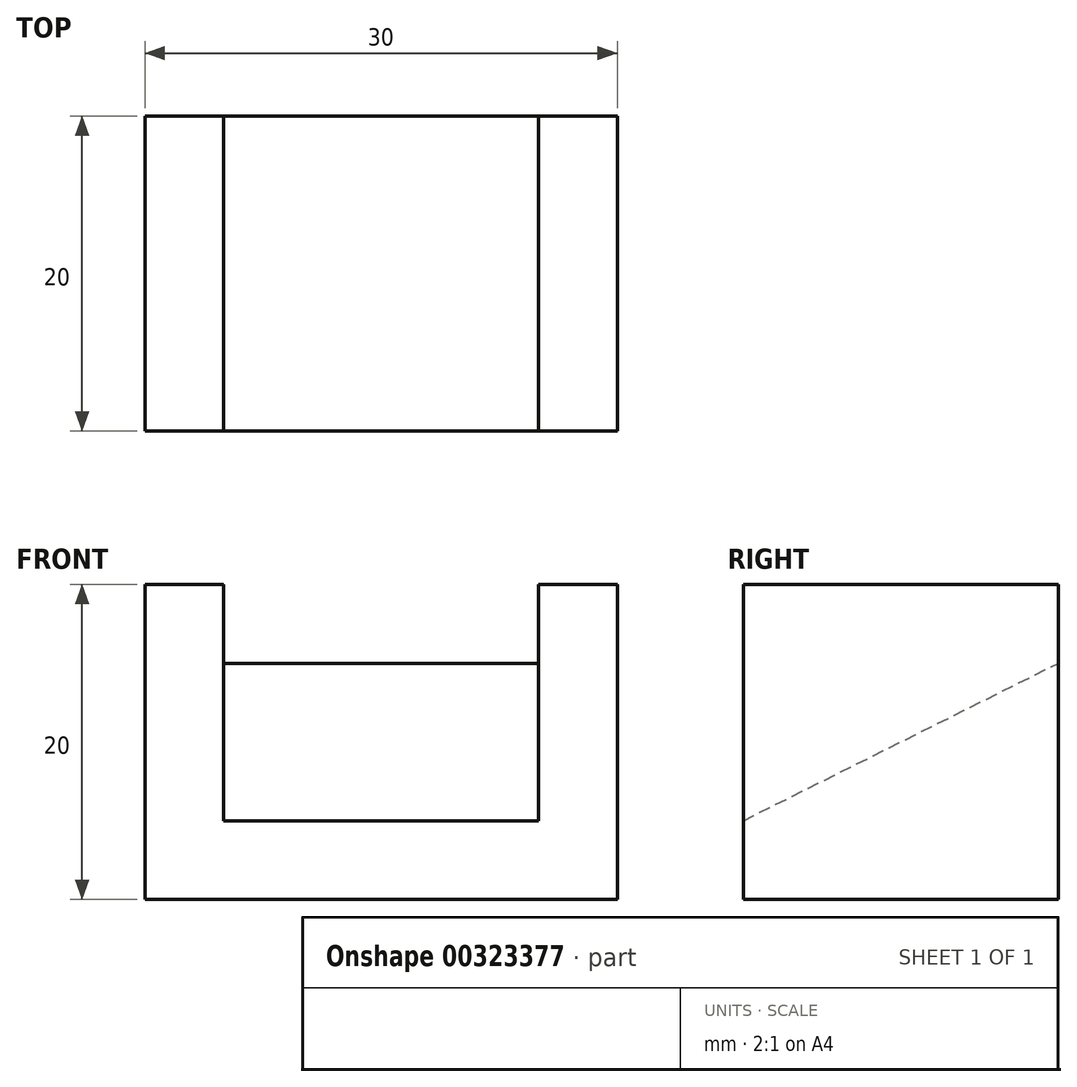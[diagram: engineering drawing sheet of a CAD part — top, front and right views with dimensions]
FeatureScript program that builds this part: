
annotation { "Feature Type Name" : "Feature", "Feature Type Description" : "" }
export const myFeature = defineFeature(function(context is Context, id is Id, definition is map)
    precondition{}
    {
        {
            var Q0;
            Q0=qCreatedBy(makeId("Front.planeOp"),FACE);
            var sketch = newSketch(context, id + "F0", { "sketchPlane" : qUnion([Q0])});
            skLineSegment(sketch, "E0.bottom", {"start": v(0, 0) * mm, "end": v(30, 0) * mm});
            skLineSegment(sketch, "E0.top", {"start": v(0, 20) * mm, "end": v(30, 20) * mm});
            skLineSegment(sketch, "E0.left", {"start": v(0, 0) * mm, "end": v(0, 20) * mm});
            skLineSegment(sketch, "E0.right", {"start": v(30, 0) * mm, "end": v(30, 20) * mm});
            skSolve(sketch);
        }
        {
            var Q0;
            Q0 = qSketchRegion(id + "F0", true);
            extrude(context, id + "F1", {"entities" : qUnion([Q0]), "depth" : 20 * mm});
        }
        {
            var Q0;
            Q0=makeQuery(id+"F1.opExtrude","CAP_FACE",FACE,{"disambiguationData":[OSD([sQuery(id+"F0.wireOp",EDGE,"E0.bottom"),sQuery(id+"F0.wireOp",EDGE,"E0.top"),sQuery(id+"F0.wireOp",EDGE,"E0.left"),sQuery(id+"F0.wireOp",EDGE,"E0.right")])],"isStart":false});
            var sketch = newSketch(context, id + "F2", { "sketchPlane" : qUnion([Q0])});
            skLineSegment(sketch, "E1", {"start": v(5, 20) * mm, "end": v(5, 5) * mm});
            skLineSegment(sketch, "E2", {"start": v(5, 5) * mm, "end": v(25, 5) * mm});
            skLineSegment(sketch, "E3", {"start": v(25, 5) * mm, "end": v(25, 20) * mm});
            skSolve(sketch);
        }
        {
            var Q0;
            Q0 = qSketchRegion(id + "F2", true);
            var Q1;
            {var subQ0=sQuery(id+"F2.wireOp",EDGE,"E1");Q1=makeQuery(id+"F2.imprint","IMPRINT",FACE,{"disambiguationData":[TD([[makeQuery(id+"F2.imprint","IMPRINT",EDGE,{"derivedFrom":subQ0}),1.0]])]});}
            extrude(context, id + "F3", {"entities" : qUnion([Q0, Q1]), "operationType" : NewBodyOperationType.REMOVE, "oppositeDirection" : true, "depth" : 25 * mm});
        }
        {
            var Q0;
            Q0=makeQuery(id+"F3.boolean.opBoolean","COPY",FACE,{"derivedFrom":makeQuery(id+"F3.opExtrude","SWEPT_FACE",FACE,{"disambiguationData":[OSD([sQuery(id+"F2.wireOp",EDGE,"E1")])]})});
            var sketch = newSketch(context, id + "F4", { "sketchPlane" : qUnion([Q0])});
            skLineSegment(sketch, "E4", {"start": v(-20, 5) * mm, "end": v(0, 15) * mm});
            skSolve(sketch);
        }
        {
            var Q0;
            Q0 = qSketchRegion(id + "F4", true);
            var Q1;
            {var subQ0=sQuery(id+"F4.wireOp",EDGE,"E4");Q1=makeQuery(id+"F4.imprint","IMPRINT",FACE,{"disambiguationData":[TD([[makeQuery(id+"F4.imprint","IMPRINT",EDGE,{"derivedFrom":subQ0}),-1.0]])]});}
            var Q2;
            Q2=makeQuery(id+"F3.boolean.opBoolean","COPY",FACE,{"derivedFrom":makeQuery(id+"F3.opExtrude","SWEPT_FACE",FACE,{"disambiguationData":[OSD([sQuery(id+"F2.wireOp",EDGE,"E3")])]})});
            extrude(context, id + "F5", {"entities" : qUnion([Q0, Q1]), "operationType" : NewBodyOperationType.ADD, "endBound" : BoundingType.UP_TO_SURFACE, "endBoundEntityFace" : qUnion([Q2]), "depth" : 25 * mm});
        }
    });
